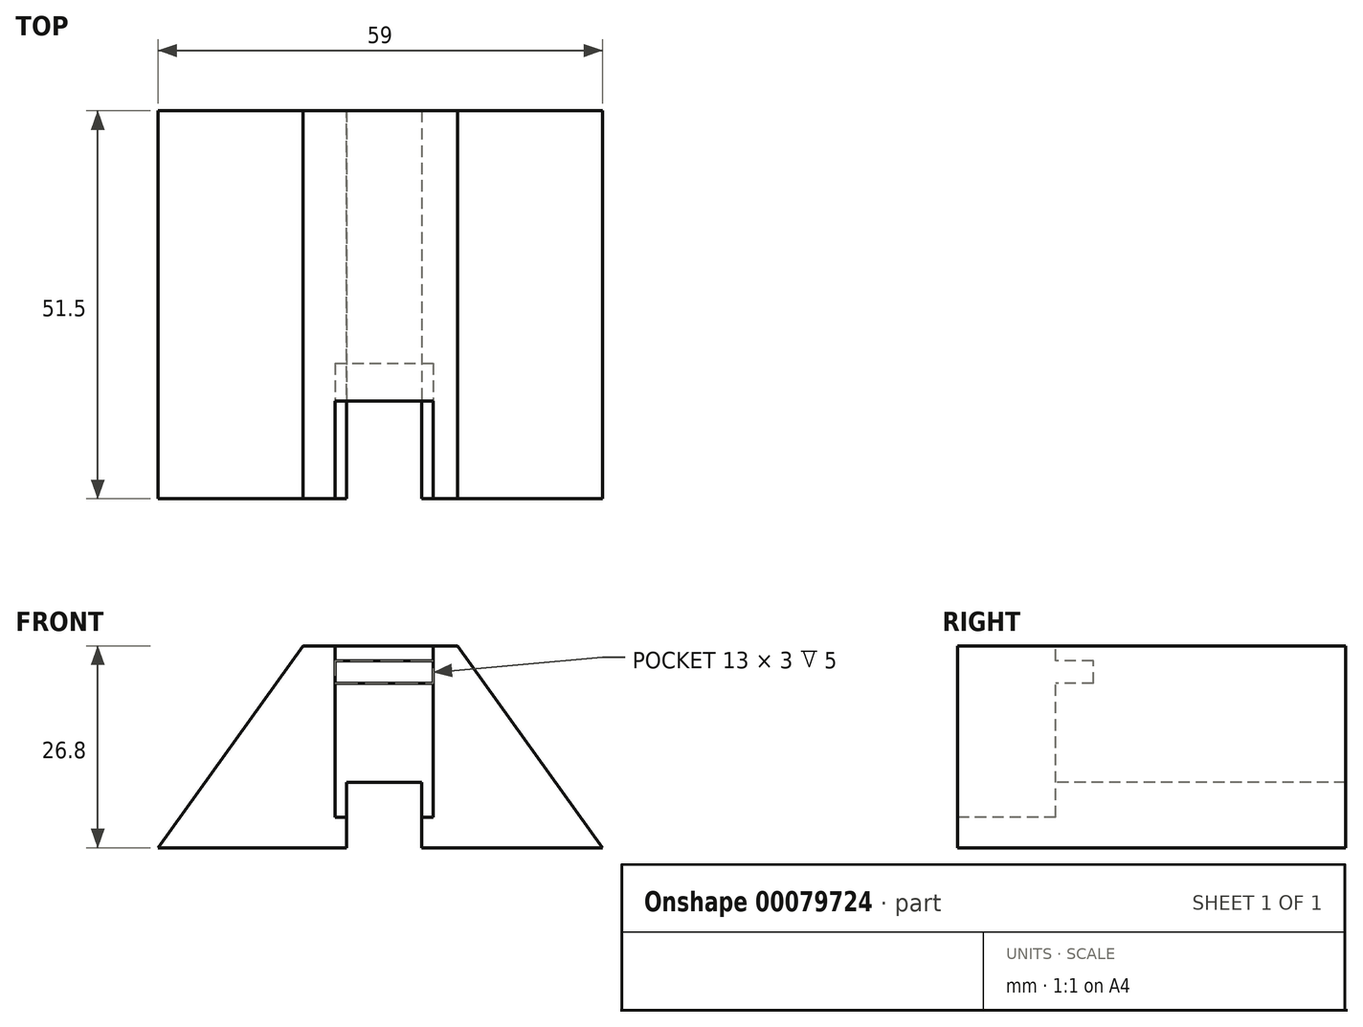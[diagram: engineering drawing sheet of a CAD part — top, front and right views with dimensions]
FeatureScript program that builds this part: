
annotation { "Feature Type Name" : "Feature", "Feature Type Description" : "" }
export const myFeature = defineFeature(function(context is Context, id is Id, definition is map)
    precondition{}
    {
        {
            var Q0;
            Q0=qCreatedBy(makeId("Front.planeOp"),FACE);
            var sketch = newSketch(context, id + "F0", { "sketchPlane" : qUnion([Q0])});
            skLineSegment(sketch, "E0", {"start": v(-29.5, -13.4) * mm, "end": v(-10.25, 13.4) * mm});
            skLineSegment(sketch, "E1", {"start": v(-10.25, 13.4) * mm, "end": v(10.25, 13.4) * mm});
            skLineSegment(sketch, "E2", {"start": v(10.25, 13.4) * mm, "end": v(29.5, -13.4) * mm});
            skLineSegment(sketch, "E3", {"start": v(29.5, -13.4) * mm, "end": v(-29.5, -13.4) * mm});
            skSolve(sketch);
        }
        {
            var Q0;
            Q0 = qSketchRegion(id + "F0", true);
            extrude(context, id + "F1", {"entities" : qUnion([Q0]), "depth" : 51.5 * mm});
        }
        {
            var Q0;
            Q0=makeQuery(id+"F1.opExtrude","SWEPT_FACE",FACE,{"disambiguationData":[OSD([sQuery(id+"F0.wireOp",EDGE,"E1")])]});
            var sketch = newSketch(context, id + "F2", { "sketchPlane" : qUnion([Q0])});
            skLineSegment(sketch, "E4.bottom", {"start": v(-6, -51.5) * mm, "end": v(7, -51.5) * mm});
            skLineSegment(sketch, "E4.top", {"start": v(-6, -38.5) * mm, "end": v(7, -38.5) * mm});
            skLineSegment(sketch, "E4.left", {"start": v(-6, -51.5) * mm, "end": v(-6, -38.5) * mm});
            skLineSegment(sketch, "E4.right", {"start": v(7, -51.5) * mm, "end": v(7, -38.5) * mm});
            skSolve(sketch);
        }
        {
            var Q0;
            Q0 = qSketchRegion(id + "F2", true);
            extrude(context, id + "F3", {"entities" : qUnion([Q0]), "operationType" : NewBodyOperationType.REMOVE, "oppositeDirection" : true, "depth" : 22.75 * mm});
        }
        {
            var Q0;
            Q0=makeQuery(id+"F3.boolean.opBoolean","COPY",FACE,{"derivedFrom":makeQuery(id+"F3.opExtrude","CAP_FACE",FACE,{"disambiguationData":[OSD([sQuery(id+"F2.wireOp",EDGE,"E4.bottom"),sQuery(id+"F2.wireOp",EDGE,"E4.top"),sQuery(id+"F2.wireOp",EDGE,"E4.left"),sQuery(id+"F2.wireOp",EDGE,"E4.right")])],"isStart":false})});
            var sketch = newSketch(context, id + "F4", { "sketchPlane" : qUnion([Q0])});
            skLineSegment(sketch, "E5.bottom", {"start": v(-4.5, -38.5) * mm, "end": v(5.5, -38.5) * mm});
            skLineSegment(sketch, "E5.top", {"start": v(-4.5, -51.5) * mm, "end": v(5.5, -51.5) * mm});
            skLineSegment(sketch, "E5.left", {"start": v(-4.5, -38.5) * mm, "end": v(-4.5, -51.5) * mm});
            skLineSegment(sketch, "E5.right", {"start": v(5.5, -38.5) * mm, "end": v(5.5, -51.5) * mm});
            skSolve(sketch);
        }
        {
            var Q0;
            Q0 = qSketchRegion(id + "F4", true);
            extrude(context, id + "F5", {"entities" : qUnion([Q0]), "operationType" : NewBodyOperationType.REMOVE, "oppositeDirection" : true, "depth" : 4.05 * mm});
        }
        {
            var Q0;
            Q0=makeQuery(id+"F5.boolean.opBoolean","MERGE",FACE,{"derivedFrom":[makeQuery(id+"F3.boolean.opBoolean","COPY",FACE,{"derivedFrom":makeQuery(id+"F3.opExtrude","SWEPT_FACE",FACE,{"disambiguationData":[OSD([sQuery(id+"F2.wireOp",EDGE,"E4.top")])]})}),makeQuery(id+"F5.opExtrude","SWEPT_FACE",FACE,{"disambiguationData":[OSD([sQuery(id+"F4.wireOp",EDGE,"E5.bottom")])]})]});
            var sketch = newSketch(context, id + "F6", { "sketchPlane" : qUnion([Q0])});
            skLineSegment(sketch, "E6", {"start": v(0, 30.12) * mm, "end": v(0, -21.36) * mm, "construction": true});
            skLineSegment(sketch, "E7.bottom", {"start": v(-6, 11.4) * mm, "end": v(7, 11.4) * mm});
            skLineSegment(sketch, "E7.top", {"start": v(-6, 8.4) * mm, "end": v(7, 8.4) * mm});
            skLineSegment(sketch, "E7.left", {"start": v(-6, 11.4) * mm, "end": v(-6, 8.4) * mm});
            skLineSegment(sketch, "E7.right", {"start": v(7, 11.4) * mm, "end": v(7, 8.4) * mm});
            skSolve(sketch);
        }
        {
            var Q0;
            Q0=makeQuery(id+"F6.imprint","IMPRINT",FACE,{"disambiguationData":[TD([[makeQuery(id+"F6.imprint","IMPRINT",EDGE,{"derivedFrom":sQuery(id+"F6.wireOp",EDGE,"E7.bottom")}),-1.0]])]});
            extrude(context, id + "F7", {"entities" : qUnion([Q0]), "operationType" : NewBodyOperationType.REMOVE, "oppositeDirection" : true, "depth" : 5 * mm});
        }
        {
            var Q0;
            {var subQ2=sQuery(id+"F2.wireOp",EDGE,"E4.top");Q0=makeQuery(id+"F7.boolean.opBoolean","SPLIT",FACE,{"disambiguationData":[TD([makeQuery(id+"F1.opExtrude","SWEPT_FACE",FACE,{"disambiguationData":[OSD([sQuery(id+"F0.wireOp",EDGE,"E3")])]})])],"derivedFrom":makeQuery(id+"F5.boolean.opBoolean","MERGE",FACE,{"derivedFrom":[makeQuery(id+"F3.boolean.opBoolean","COPY",FACE,{"derivedFrom":makeQuery(id+"F3.opExtrude","SWEPT_FACE",FACE,{"disambiguationData":[OSD([subQ2])]})}),makeQuery(id+"F5.opExtrude","SWEPT_FACE",FACE,{"disambiguationData":[OSD([sQuery(id+"F4.wireOp",EDGE,"E5.bottom")])]})]})});}
            var sketch = newSketch(context, id + "F8", { "sketchPlane" : qUnion([Q0])});
            skLineSegment(sketch, "E8.bottom", {"start": v(-4.5, -13.4) * mm, "end": v(5.5, -13.4) * mm});
            skLineSegment(sketch, "E8.top", {"start": v(-4.5, -4.73) * mm, "end": v(5.5, -4.73) * mm});
            skLineSegment(sketch, "E8.left", {"start": v(-4.5, -13.4) * mm, "end": v(-4.5, -4.73) * mm});
            skLineSegment(sketch, "E8.right", {"start": v(5.5, -13.4) * mm, "end": v(5.5, -4.73) * mm});
            skLineSegment(sketch, "E9.bottom", {"start": v(5.5, -13.4) * mm, "end": v(5.5, -13.4) * mm});
            skLineSegment(sketch, "E9.top", {"start": v(5.5, -13.4) * mm, "end": v(5.5, -13.4) * mm});
            skLineSegment(sketch, "E9.left", {"start": v(5.5, -13.4) * mm, "end": v(5.5, -13.4) * mm});
            skLineSegment(sketch, "E9.right", {"start": v(5.5, -13.4) * mm, "end": v(5.5, -13.4) * mm});
            skSolve(sketch);
        }
        {
            var Q0;
            Q0 = qSketchRegion(id + "F8", true);
            extrude(context, id + "F9", {"entities" : qUnion([Q0]), "operationType" : NewBodyOperationType.REMOVE, "oppositeDirection" : true, "depth" : 51.5 * mm});
        }
    });
